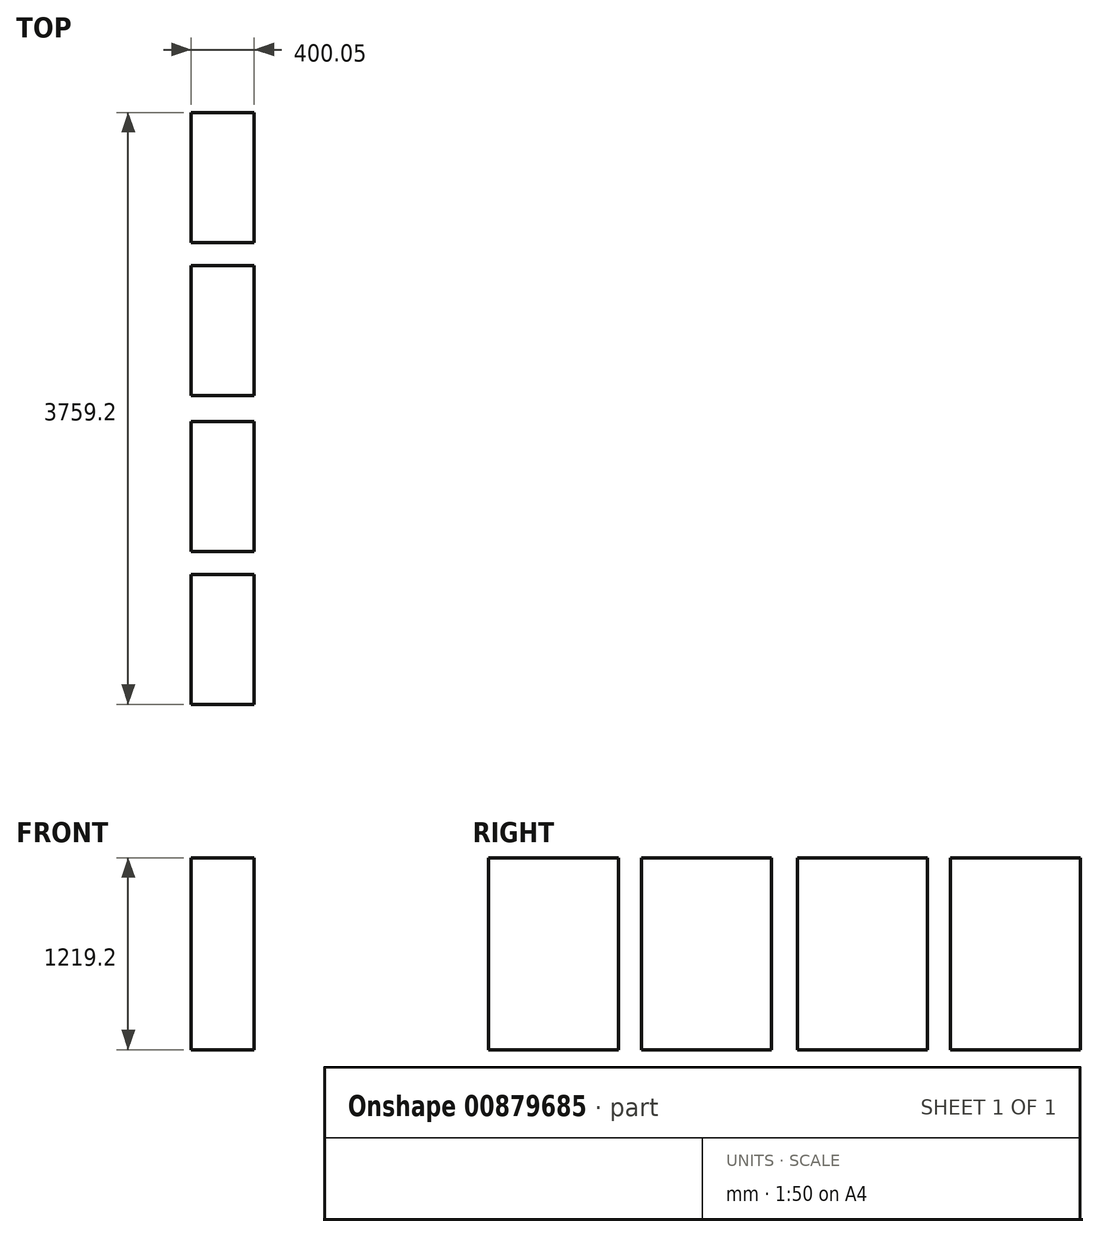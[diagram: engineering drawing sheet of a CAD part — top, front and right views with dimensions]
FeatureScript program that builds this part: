
annotation { "Feature Type Name" : "Feature", "Feature Type Description" : "" }
export const myFeature = defineFeature(function(context is Context, id is Id, definition is map)
    precondition{}
    {
        {
            var Q0;
            Q0=qCreatedBy(makeId("Top.planeOp"),FACE);
            var sketch = newSketch(context, id + "F0", { "sketchPlane" : qUnion([Q0])});
            skLineSegment(sketch, "E0.bottom", {"start": v(544.5, 1065.1) * mm, "end": v(944.56, 1065.1) * mm});
            skLineSegment(sketch, "E0.top", {"start": v(544.5, 239.6) * mm, "end": v(944.56, 239.6) * mm});
            skLineSegment(sketch, "E0.left", {"start": v(544.5, 1065.1) * mm, "end": v(544.5, 239.6) * mm});
            skLineSegment(sketch, "E0.right", {"start": v(944.56, 1065.1) * mm, "end": v(944.56, 239.6) * mm});
            skLineSegment(sketch, "E1.bottom", {"start": v(544.5, 93.56) * mm, "end": v(944.56, 93.56) * mm});
            skLineSegment(sketch, "E1.top", {"start": v(544.5, -731.94) * mm, "end": v(944.56, -731.94) * mm});
            skLineSegment(sketch, "E1.left", {"start": v(544.5, 93.56) * mm, "end": v(544.5, -731.94) * mm});
            skLineSegment(sketch, "E1.right", {"start": v(944.56, 93.56) * mm, "end": v(944.56, -731.94) * mm});
            skLineSegment(sketch, "E2.bottom", {"start": v(544.5, -897.04) * mm, "end": v(944.56, -897.04) * mm});
            skLineSegment(sketch, "E2.top", {"start": v(544.5, -1722.54) * mm, "end": v(944.56, -1722.54) * mm});
            skLineSegment(sketch, "E2.left", {"start": v(544.5, -897.04) * mm, "end": v(544.5, -1722.54) * mm});
            skLineSegment(sketch, "E2.right", {"start": v(944.56, -897.04) * mm, "end": v(944.56, -1722.54) * mm});
            skLineSegment(sketch, "E3.bottom", {"start": v(544.5, -1868.6) * mm, "end": v(944.56, -1868.6) * mm});
            skLineSegment(sketch, "E3.top", {"start": v(544.5, -2694.1) * mm, "end": v(944.56, -2694.1) * mm});
            skLineSegment(sketch, "E3.left", {"start": v(544.5, -1868.6) * mm, "end": v(544.5, -2694.1) * mm});
            skLineSegment(sketch, "E3.right", {"start": v(944.56, -1868.6) * mm, "end": v(944.56, -2694.1) * mm});
            skSolve(sketch);
        }
        {
            var Q0;
            Q0=makeQuery(id+"F0.imprint","IMPRINT",FACE,{"disambiguationData":[TD([[makeQuery(id+"F0.imprint","IMPRINT",EDGE,{"derivedFrom":sQuery(id+"F0.wireOp",EDGE,"E0.bottom")}),-1.0]])]});
            var Q1;
            Q1=makeQuery(id+"F0.imprint","IMPRINT",FACE,{"disambiguationData":[TD([[makeQuery(id+"F0.imprint","IMPRINT",EDGE,{"derivedFrom":sQuery(id+"F0.wireOp",EDGE,"E1.bottom")}),-1.0]])]});
            var Q2;
            Q2=makeQuery(id+"F0.imprint","IMPRINT",FACE,{"disambiguationData":[TD([[makeQuery(id+"F0.imprint","IMPRINT",EDGE,{"derivedFrom":sQuery(id+"F0.wireOp",EDGE,"E2.bottom")}),-1.0]])]});
            var Q3;
            Q3=makeQuery(id+"F0.imprint","IMPRINT",FACE,{"disambiguationData":[TD([[makeQuery(id+"F0.imprint","IMPRINT",EDGE,{"derivedFrom":sQuery(id+"F0.wireOp",EDGE,"E3.bottom")}),-1.0]])]});
            extrude(context, id + "F1", {"entities" : qUnion([Q0, Q1, Q2, Q3]), "depth" : 1219.2 * mm, "offsetDistance" : 25.4 * mm});
        }
    });
